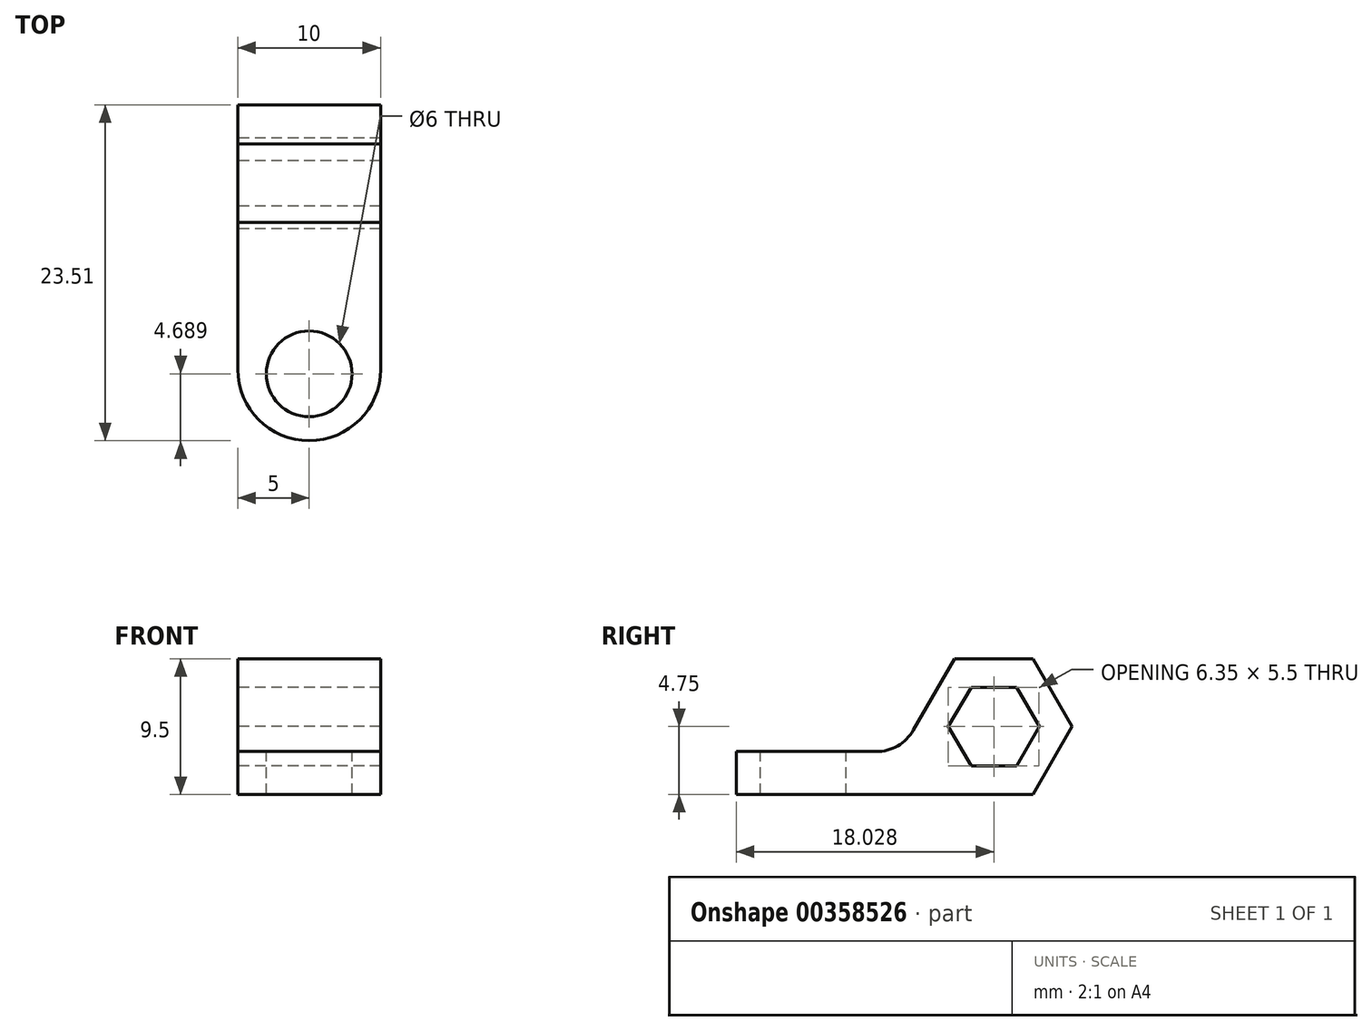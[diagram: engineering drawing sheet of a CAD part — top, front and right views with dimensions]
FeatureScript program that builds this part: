
annotation { "Feature Type Name" : "Feature", "Feature Type Description" : "" }
export const myFeature = defineFeature(function(context is Context, id is Id, definition is map)
    precondition{}
    {
        {
            var Q0;
            Q0=qCreatedBy(makeId("Right.planeOp"),FACE);
            var sketch = newSketch(context, id + "F0", { "sketchPlane" : qUnion([Q0])});
            skLineSegment(sketch, "E0.bottom", {"start": v(0, 0) * mm, "end": v(-20.77, 0) * mm});
            skLineSegment(sketch, "E0.top", {"start": v(0, 9.5) * mm, "end": v(-5.48, 9.5) * mm});
            skLineSegment(sketch, "E0.right", {"start": v(-20.77, 0) * mm, "end": v(-20.77, 3) * mm});
            skCircle(sketch, "E1.cCircle", {"center": v(-2.74, 4.75) * mm, "radius": 2.75 * mm, "construction": true});
            skLineSegment(sketch, "E1.0", {"start": v(-5.92, 4.75) * mm, "end": v(-4.33, 7.5) * mm});
            skLineSegment(sketch, "E1.1", {"start": v(-4.33, 7.5) * mm, "end": v(-1.15, 7.5) * mm});
            skLineSegment(sketch, "E1.2", {"start": v(-1.15, 7.5) * mm, "end": v(0.43, 4.75) * mm});
            skLineSegment(sketch, "E1.3", {"start": v(0.43, 4.75) * mm, "end": v(-1.15, 2) * mm});
            skLineSegment(sketch, "E1.4", {"start": v(-1.15, 2) * mm, "end": v(-4.33, 2) * mm});
            skLineSegment(sketch, "E1.5", {"start": v(-4.33, 2) * mm, "end": v(-5.92, 4.75) * mm});
            skPoint(sketch, "E1.0.midPoint", {"position": v(-5.12, 6.13) * mm});
            skLineSegment(sketch, "E2.0", {"start": v(2.74, 4.75) * mm, "end": v(0, 0) * mm});
            skLineSegment(sketch, "E2.1", {"start": v(0, 9.5) * mm, "end": v(2.74, 4.75) * mm});
            skLineSegment(sketch, "E3.0", {"start": v(-8.37, 4.5) * mm, "end": v(-5.48, 9.5) * mm});
            skLineSegment(sketch, "E4", {"start": v(-8.37, 4.5) * mm, "end": v(-8.37, 3) * mm});
            skLineSegment(sketch, "E5", {"start": v(-8.37, 3) * mm, "end": v(-20.77, 3) * mm});
            skSolve(sketch);
        }
        {
            var Q0;
            Q0=qSketchRegion(id+"F0",true);
            extrude(context, id + "F1", {"entities" : qUnion([Q0]), "depth" : 10 * mm});
        }
        {
            var Q0;
            Q0=makeQuery(id+"F1.opExtrude","SWEPT_FACE",FACE,{"disambiguationData":[OSD([sQuery(id+"F0.wireOp",EDGE,"E5")])]});
            var sketch = newSketch(context, id + "F2", { "sketchPlane" : qUnion([Q0])});
            skCircle(sketch, "E6", {"center": v(5, -16.08) * mm, "radius": 3 * mm});
            skPoint(sketch, "E7", {"position": v(5, -20.77) * mm});
            skSolve(sketch);
        }
        {
            var Q0;
            Q0=qSketchRegion(id+"F2",true);
            extrude(context, id + "F3", {"entities" : qUnion([Q0]), "operationType" : NewBodyOperationType.REMOVE, "oppositeDirection" : true, "depth" : 25 * mm});
        }
        {
            var Q0;
            Q0=makeQuery(id+"F1.opExtrude","CAP_EDGE",EDGE,{"disambiguationData":[OSD([sQuery(id+"F0.wireOp",EDGE,"E0.right")])],"isStart":true});
            var Q1;
            Q1=makeQuery(id+"F1.opExtrude","CAP_EDGE",EDGE,{"disambiguationData":[OSD([sQuery(id+"F0.wireOp",EDGE,"E0.right")])],"isStart":false});
            fillet(context, id + "F4", {"entities" : qUnion([Q0, Q1]), "radius" : 5 * mm, "tangentPropagation" : true, "allowEdgeOverflow" : false});
        }
        {
            var Q0;
            Q0=makeQuery(id+"F1.opExtrude","SWEPT_EDGE",EDGE,{"disambiguationData":[OSD([sQuery(id+"F0.wireOp",EDGE,"E4"),sQuery(id+"F0.wireOp",EDGE,"E5")])]});
            fillet(context, id + "F5", {"entities" : qUnion([Q0]), "radius" : 3 * mm, "tangentPropagation" : true, "allowEdgeOverflow" : false});
        }
    });
